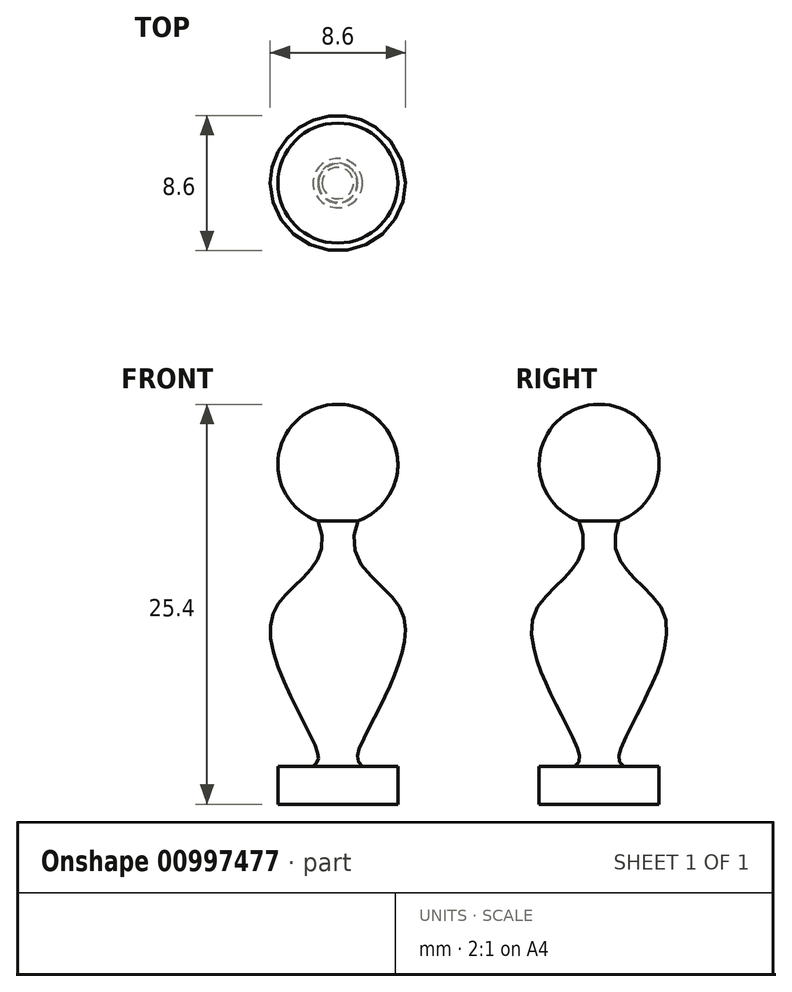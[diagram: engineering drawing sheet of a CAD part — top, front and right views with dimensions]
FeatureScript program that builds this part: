
annotation { "Feature Type Name" : "Feature", "Feature Type Description" : "" }
export const myFeature = defineFeature(function(context is Context, id is Id, definition is map)
    precondition{}
    {
        {
            var Q0;
            Q0=qCreatedBy(makeId("Front.planeOp"),FACE);
            var sketch = newSketch(context, id + "F0", { "sketchPlane" : qUnion([Q0])});
            skLineSegment(sketch, "E0", {"start": v(0, 0) * mm, "end": v(0, 25.4) * mm});
            skLineSegment(sketch, "E1", {"start": v(0, 0) * mm, "end": v(3.81, 0) * mm});
            skPoint(sketch, "E2", {"position": v(0, 17.78) * mm});
            skArc(sketch, "E3", {"start": v(1.27, 18) * mm, "mid": v(3.76, 22.23) * mm, "end": v(0, 25.4) * mm});
            skPoint(sketch, "E4", {"position": v(1.27, 18) * mm});
            skPoint(sketch, "E5.1.internal.snap0", {"position": v(0, 12.7) * mm});
            skFitSpline(sketch, "E5", {"points": [v(1.27, 18) * mm, v(4.2, 11.85) * mm, v(1.27, 3.23) * mm, v(3.81, 0) * mm], "startDerivative": vector(-11.18, -28) * mm, "endDerivative": vector(19.57, -29.24) * mm});
            skPoint(sketch, "E6.orphan", {"position": v(0, 2.58) * mm});
            skLineSegment(sketch, "E7", {"start": v(3.81, 0) * mm, "end": v(3.81, 2.4) * mm});
            skLineSegment(sketch, "E8", {"start": v(3.81, 2.4) * mm, "end": v(1.57, 2.4) * mm});
            skSolve(sketch);
        }
        {
            var Q0;
            Q0 = qSketchRegion(id + "F0", true);
            var Q1;
            Q1=sQuery(id+"F0.wireOp",EDGE,"E0");
            revolve(context, id + "F1", {"surfaceOperationType" : NewSurfaceOperationType.NEW, "entities" : qUnion([Q0]), "axis" : qUnion([Q1]), "revolveType" : RevolveType.FULL});
        }
    });
